# Revit family: ASH_Contour21_S2168_BIM_GB
name_source: partatom
category: Plumbing Fixtures
revit_build: Autodesk Revit MEP 2014 (Build: 20130308_1515(x64)
units: mm (PartAtom-declared; Revit-internal decimal feet)

## types (1)
- S216801 - Contour21 Washabsin 600 x 550mm - Overflow - 1 Taphole
    Accessories = www.idealspec.co.uk
    AreaUnits = millimeters
    Assembly Code = C1030200
    AssetType = Fixed
    BIMObjectName = ASH_ArmitageShanks_WallHungWashBasins_Contour21_S2168
    BarCode = 5017830379867
    Brand = Armitage Shanks
    CWFU = 0
    CodePerformance = Vitreous china to BS 3402, BS EN 997 & BS EN 33
    Color = White
    ConnectionType = Plumbing
    Cost = 0 $
    Default Elevation = 800 mm  [stored 2.62467 ft]
    Description = Contour21 washbasin 600 x 550mm, overflow, 1 taphole
    DrainSize = 32 mm
    DurationUnit = year
    ECA = No
    ExpectedLife = 30
    Features = washbasin 600 x 550mm, overflow, 1 taphole
    Finish = White
    HWFU = 0
    IfcExportAs = IfcSanitaryType
    IfcExportType = WASHHANDBASIN
    InstallationInstructions = www.idealspec.co.uk/resources.html
    LinearUnits = millimeters
    ManufacturerURL = www.idealspec.co.uk
    Material = Vitreous china
    Model = S216801
    ModelNumber = S216801
    ModelReference = Contour21 washbasin 600 x 550mm, overflow, 1 taphole
    NBSDescription = WallHungWashBasins
    NBSReference = 45-35-70/369
    Name = WallHungWashBasins_Contour21_S2168_ArmitageShanks
    NettWeight = 17.59 Kg
    NominalDepth = 545 mm  [stored 1.78806 ft]
    NominalHeight = 173 mm  [stored 0.567585 ft]
    NominalLength = 545 mm  [stored 1.78806 ft]
    NominalWidth = 600 mm
    ProductInformation = www.idealspec.co.uk/assets/datasheet/S216801
    Shape = Sculptured
    Size = 600 x 545 x 173 mm
    Space = Internal
    URL = www.idealspec.co.uk
    Uniclass2 = Pr_40_20_96_96
    Uniclass2015Description = Wall-Hung Wash Basins
    Uniclass2015Reference = Pr_40_20_96_96
    Uniclass2015Version = Products v1.1
    Version = 1
    VolumeUnits = Litres
    WFU = 0
    WRAS = No
    WarrantyDescription = Manufacturers Warranty
    WarrantyDurationParts = 99
    WarrantyDurationUnit = year
    WashHandBasinMounting = Wall hung
    WashHandBasinType = Hand Rinse
    WaterEfficientProduct = No

note: [stored X ft] marks values corroborated as IEEE doubles in the binary element streams (Revit-internal decimal feet)

## geometry (parser evidence)
native form markers: Sweep x4
no freeform markers — native parametric forms only
